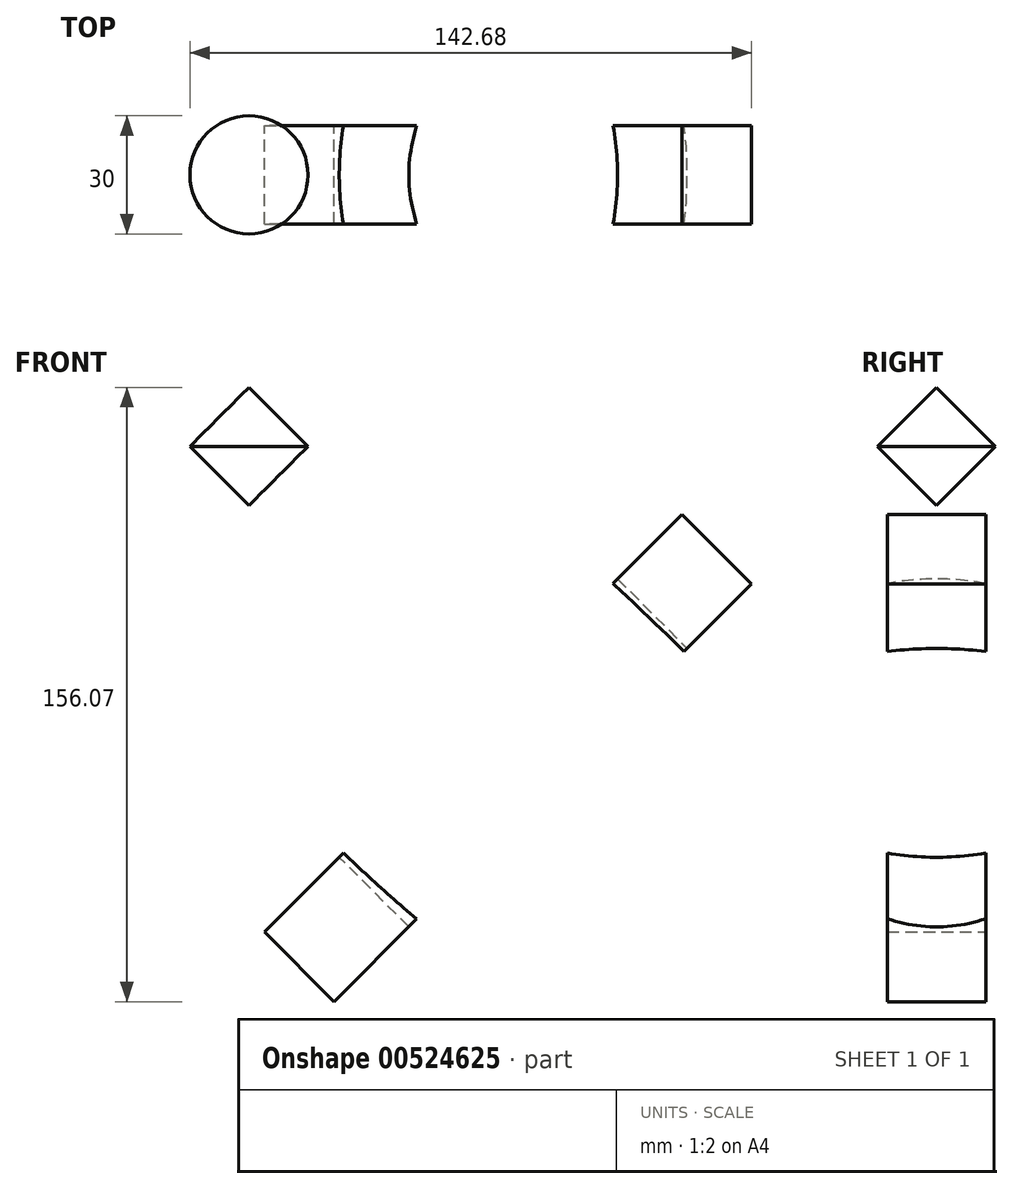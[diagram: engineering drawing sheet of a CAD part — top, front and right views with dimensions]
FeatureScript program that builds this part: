
annotation { "Feature Type Name" : "Feature", "Feature Type Description" : "" }
export const myFeature = defineFeature(function(context is Context, id is Id, definition is map)
    precondition{}
    {
        {
            var Q0;
            Q0=qCreatedBy(makeId("Front.planeOp"),FACE);
            var sketch = newSketch(context, id + "F0", { "sketchPlane" : qUnion([Q0])});
            skLineSegment(sketch, "E0", {"start": v(0, 80.4) * mm, "end": v(0, -82.74) * mm, "construction": true});
            skLineSegment(sketch, "E1", {"start": v(0, 70.71) * mm, "end": v(-70.71, 0) * mm});
            skLineSegment(sketch, "E2", {"start": v(-70.71, 0) * mm, "end": v(0, -70.71) * mm});
            skLineSegment(sketch, "E3", {"start": v(0, -70.71) * mm, "end": v(0, 70.71) * mm});
            skSolve(sketch);
        }
        {
            var Q0;
            Q0=qSketchRegion(id+"F0",true);
            var Q1;
            Q1=sQuery(id+"F0.wireOp",EDGE,"E0");
            revolve(context, id + "F1", {"entities" : qUnion([Q0]), "axis" : qUnion([Q1]), "revolveType" : RevolveType.FULL});
        }
        {
            var Q0;
            Q0=qCreatedBy(makeId("Front.planeOp"),FACE);
            var sketch = newSketch(context, id + "F2", { "sketchPlane" : qUnion([Q0])});
            skLineSegment(sketch, "E4", {"start": v(-45, 70.71) * mm, "end": v(-60, 55.71) * mm});
            skLineSegment(sketch, "E5", {"start": v(-60, 55.71) * mm, "end": v(-60, 85.71) * mm});
            skLineSegment(sketch, "E6", {"start": v(-60, 85.71) * mm, "end": v(-45, 70.71) * mm});
            skLineSegment(sketch, "E7", {"start": v(-60, 47.19) * mm, "end": v(-60, 91.17) * mm, "construction": true});
            skSolve(sketch);
        }
        {
            var Q0;
            Q0=makeQuery(id+"F2.imprint","IMPRINT",FACE,{"disambiguationData":[TD([[makeQuery(id+"F2.imprint","IMPRINT",EDGE,{"derivedFrom":sQuery(id+"F2.wireOp",EDGE,"E4")}),-1.0]])]});
            var Q1;
            Q1=sQuery(id+"F2.wireOp",EDGE,"E7");
            revolve(context, id + "F3", {"entities" : qUnion([Q0]), "axis" : qUnion([Q1]), "revolveType" : RevolveType.FULL});
        }
        {
            var Q0;
            Q0=qCreatedBy(makeId("Front.planeOp"),FACE);
            var sketch = newSketch(context, id + "F4", { "sketchPlane" : qUnion([Q0])});
            skLineSegment(sketch, "E8", {"start": v(50, 53.39) * mm, "end": v(-56.07, -52.68) * mm});
            skLineSegment(sketch, "E9", {"start": v(-56.07, -52.68) * mm, "end": v(-38.39, -70.36) * mm});
            skLineSegment(sketch, "E10", {"start": v(-38.39, -70.36) * mm, "end": v(67.68, 35.71) * mm});
            skLineSegment(sketch, "E11", {"start": v(67.68, 35.71) * mm, "end": v(50, 53.39) * mm});
            skLineSegment(sketch, "E12", {"start": v(-55.42, -15.3) * mm, "end": v(-70.71, 0) * mm});
            skSolve(sketch);
        }
        {
            var Q0;
            Q0=qSketchRegion(id+"F4",true);
            extrude(context, id + "F5", {"entities" : qUnion([Q0]), "endBound" : BoundingType.SYMMETRIC, "depth" : 25 * mm, "offsetDistance" : 25 * mm});
        }
        {
            var Q0;
            Q0=makeQuery(id+"F1.opRevolve","SWEPT_BODY",BODY,{"disambiguationData":[OSD([sQuery(id+"F0.wireOp",EDGE,"E1"),sQuery(id+"F0.wireOp",EDGE,"E2"),sQuery(id+"F0.wireOp",EDGE,"E3")])]});
            var Q1;
            Q1=makeQuery(id+"F5.opExtrude","SWEPT_BODY",BODY,{"disambiguationData":[OSD([sQuery(id+"F4.wireOp",EDGE,"E8"),sQuery(id+"F4.wireOp",EDGE,"E9"),sQuery(id+"F4.wireOp",EDGE,"E10"),sQuery(id+"F4.wireOp",EDGE,"E11")])]});
            booleanBodies(context, id + "F6", {"operationType" : BooleanOperationType.SUBTRACTION, "tools" : qUnion([Q0]), "targets" : qUnion([Q1])});
        }
    });
